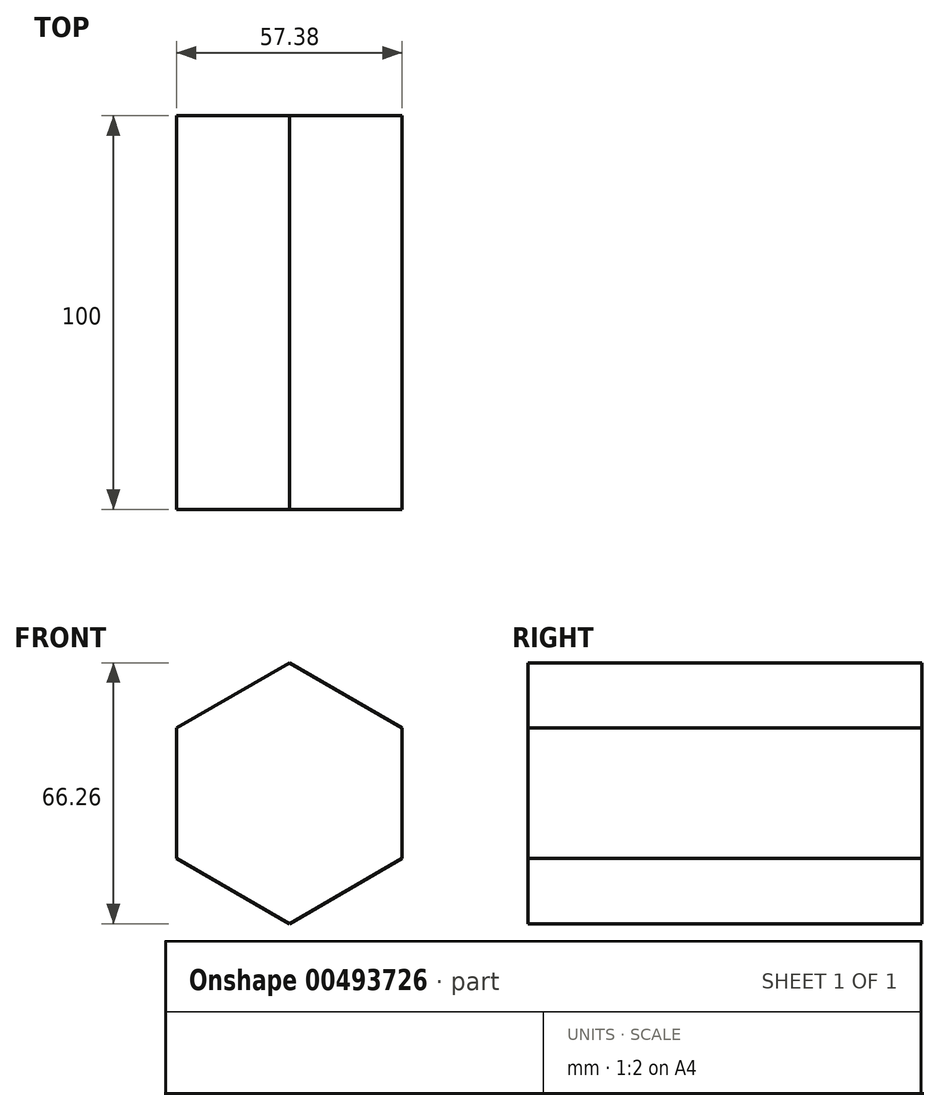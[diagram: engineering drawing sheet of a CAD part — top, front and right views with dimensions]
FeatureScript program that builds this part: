
annotation { "Feature Type Name" : "Feature", "Feature Type Description" : "" }
export const myFeature = defineFeature(function(context is Context, id is Id, definition is map)
    precondition{}
    {
        {
            var Q0;
            Q0=qCreatedBy(makeId("Front.planeOp"),FACE);
            var sketch = newSketch(context, id + "F0", { "sketchPlane" : qUnion([Q0])});
            skCircle(sketch, "E0.cCircle", {"center": v(0, 0) * mm, "radius": 33.13 * mm, "construction": true});
            skLineSegment(sketch, "E0.0", {"start": v(0, 33.13) * mm, "end": v(28.7, 16.56) * mm});
            skLineSegment(sketch, "E0.1", {"start": v(28.7, 16.56) * mm, "end": v(28.7, -16.56) * mm});
            skLineSegment(sketch, "E0.2", {"start": v(28.7, -16.56) * mm, "end": v(0, -33.13) * mm});
            skLineSegment(sketch, "E0.3", {"start": v(0, -33.13) * mm, "end": v(-28.7, -16.56) * mm});
            skLineSegment(sketch, "E0.4", {"start": v(-28.7, -16.56) * mm, "end": v(-28.7, 16.56) * mm});
            skLineSegment(sketch, "E0.5", {"start": v(-28.7, 16.56) * mm, "end": v(0, 33.13) * mm});
            skSolve(sketch);
        }
        {
            var Q0;
            Q0=makeQuery(id+"F0.imprint","IMPRINT",FACE,{"disambiguationData":[TD([[makeQuery(id+"F0.imprint","IMPRINT",EDGE,{"derivedFrom":sQuery(id+"F0.wireOp",EDGE,"E0.0")}),-1.0]])]});
            extrude(context, id + "F1", {"entities" : qUnion([Q0]), "endBound" : BoundingType.SYMMETRIC, "depth" : 100 * mm});
        }
    });
